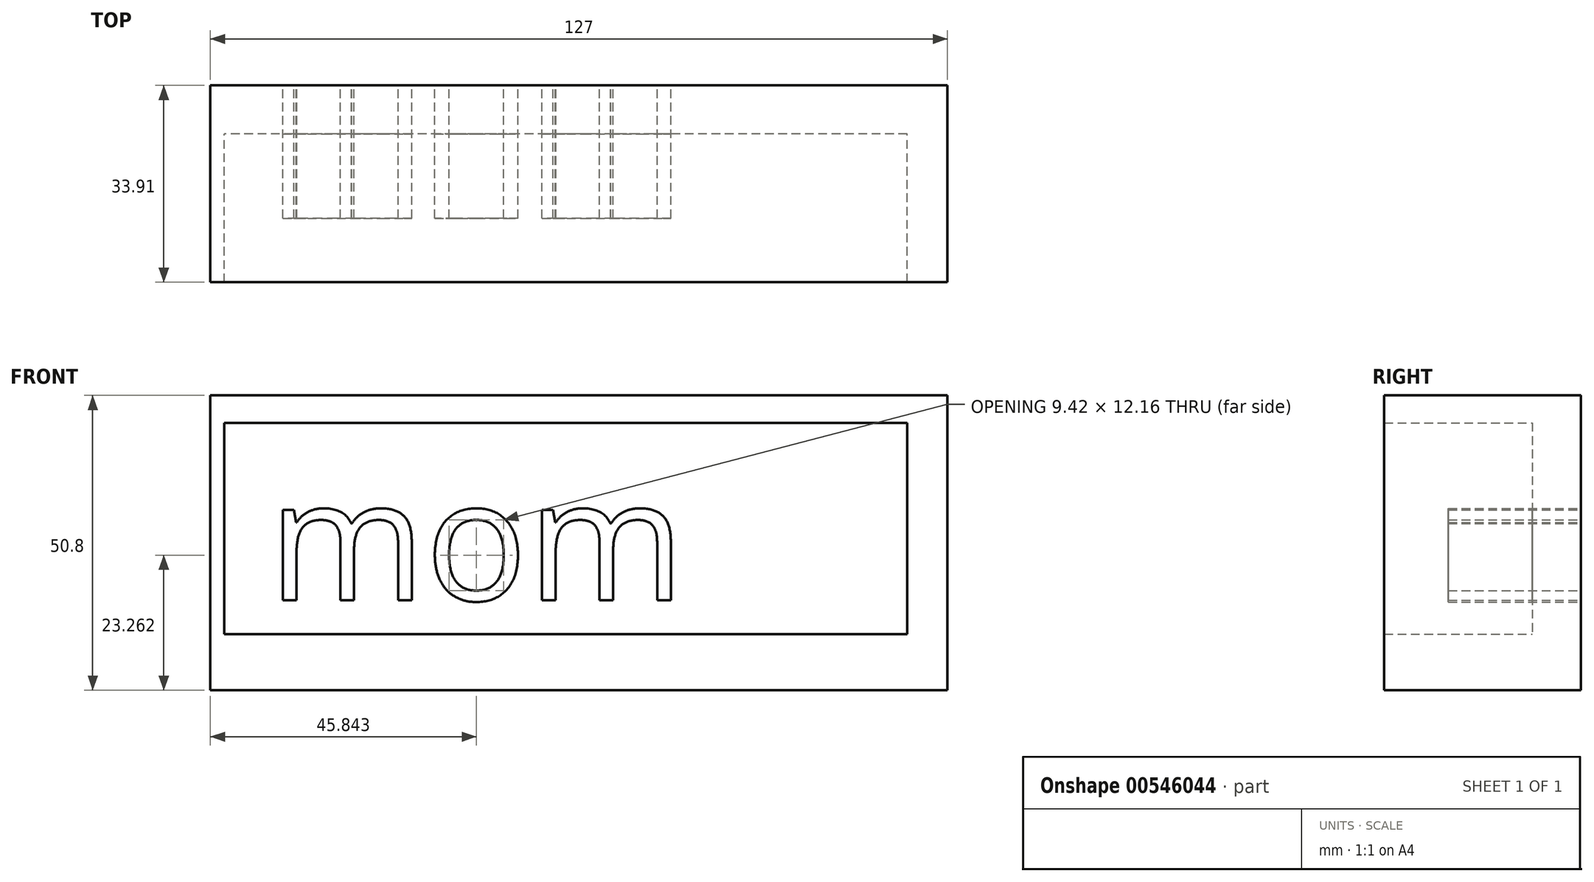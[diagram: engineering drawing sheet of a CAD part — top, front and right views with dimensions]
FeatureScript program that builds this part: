
annotation { "Feature Type Name" : "Feature", "Feature Type Description" : "" }
export const myFeature = defineFeature(function(context is Context, id is Id, definition is map)
    precondition{}
    {
        {
            var Q0;
            Q0=qCreatedBy(makeId("Front.planeOp"),FACE);
            var sketch = newSketch(context, id + "F0", { "sketchPlane" : qUnion([Q0])});
            skLineSegment(sketch, "E0.bottom", {"start": v(-55.9, 9.05) * mm, "end": v(71.1, 9.05) * mm});
            skLineSegment(sketch, "E0.top", {"start": v(-55.9, -41.75) * mm, "end": v(71.1, -41.75) * mm});
            skLineSegment(sketch, "E0.left", {"start": v(-55.9, 9.05) * mm, "end": v(-55.9, -41.75) * mm});
            skLineSegment(sketch, "E0.right", {"start": v(71.1, 9.05) * mm, "end": v(71.1, -41.75) * mm});
            skLineSegment(sketch, "E1.bottom", {"start": v(64.16, 4.33) * mm, "end": v(-53.47, 4.33) * mm});
            skLineSegment(sketch, "E1.top", {"start": v(64.16, -32.07) * mm, "end": v(-53.47, -32.07) * mm});
            skLineSegment(sketch, "E1.left", {"start": v(64.16, 4.33) * mm, "end": v(64.16, -32.07) * mm});
            skLineSegment(sketch, "E1.right", {"start": v(-53.47, 4.33) * mm, "end": v(-53.47, -32.07) * mm});
            skPoint(sketch, "E1.middle", {"position": v(5.34, -13.87) * mm});
            skSolve(sketch);
        }
        {
            var Q0;
            Q0=makeQuery(id+"F0.imprint","IMPRINT",FACE,{"disambiguationData":[TD([[makeQuery(id+"F0.imprint","IMPRINT",EDGE,{"derivedFrom":sQuery(id+"F0.wireOp",EDGE,"E0.bottom")}),-1.0]])]});
            extrude(context, id + "F1", {"entities" : qUnion([Q0]), "depth" : 33.9 * mm, "offsetDistance" : 25.4 * mm});
        }
        {
            var Q0;
            Q0=makeQuery(id+"F0.imprint","IMPRINT",FACE,{"disambiguationData":[TD([[makeQuery(id+"F0.imprint","IMPRINT",EDGE,{"derivedFrom":sQuery(id+"F0.wireOp",EDGE,"E1.bottom")}),1.0]])]});
            extrude(context, id + "F2", {"entities" : qUnion([Q0]), "operationType" : NewBodyOperationType.ADD, "depth" : 8.38 * mm, "offsetDistance" : 25.4 * mm});
        }
        {
            var Q0;
            Q0=qCreatedBy(makeId("Front.planeOp"),FACE);
            var sketch = newSketch(context, id + "F3", { "sketchPlane" : qUnion([Q0])});
            skText(sketch, "E2", { "text": "mom", "fontName": "OpenSans-Regular.ttf"});
            const initialGuessF3  = {"E2": [-0.0459, -0.02626, 1, 0, 0.02095]};
            skSetInitialGuess(sketch, initialGuessF3);
            skSolve(sketch);
        }
        {
            var Q0;
            Q0 = qSketchRegion(id + "F3", true);
            extrude(context, id + "F4", {"entities" : qUnion([Q0]), "depth" : 22.9 * mm, "offsetDistance" : 25.4 * mm});
        }
    });
